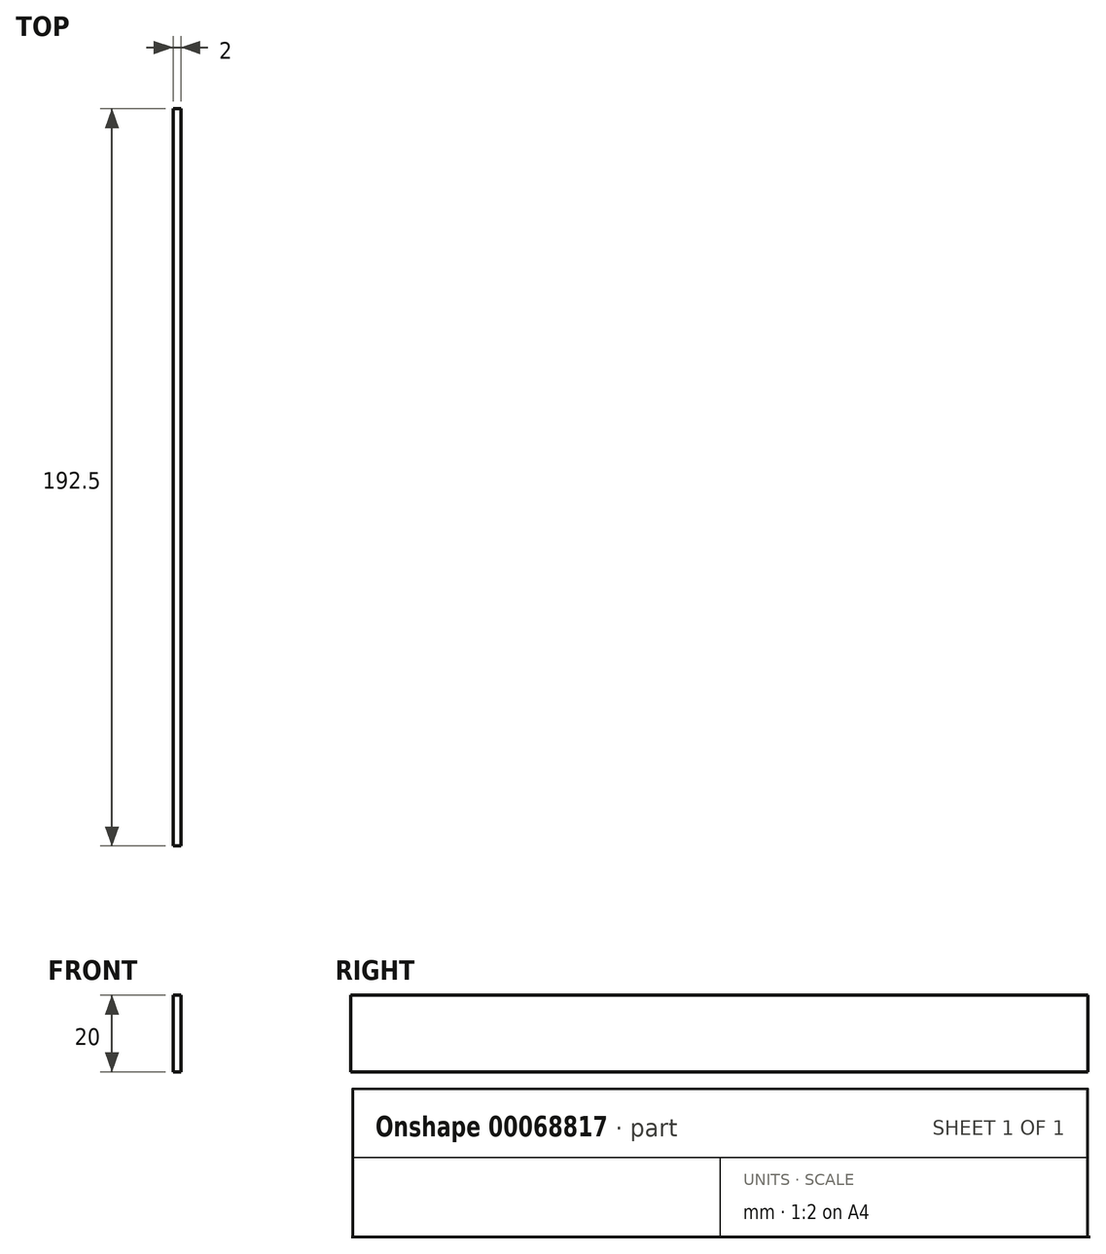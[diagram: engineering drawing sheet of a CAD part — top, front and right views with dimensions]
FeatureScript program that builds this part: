
annotation { "Feature Type Name" : "Feature", "Feature Type Description" : "" }
export const myFeature = defineFeature(function(context is Context, id is Id, definition is map)
    precondition{}
    {
        {
            var Q0;
            Q0=qCreatedBy(makeId("Right.planeOp"),FACE);
            var sketch = newSketch(context, id + "F0", { "sketchPlane" : qUnion([Q0])});
            skLineSegment(sketch, "E0.bottom", {"start": v(0, 0) * mm, "end": v(192.5, 0) * mm});
            skLineSegment(sketch, "E0.top", {"start": v(0, 20) * mm, "end": v(192.5, 20) * mm});
            skLineSegment(sketch, "E0.left", {"start": v(0, 0) * mm, "end": v(0, 20) * mm});
            skLineSegment(sketch, "E0.right", {"start": v(192.5, 0) * mm, "end": v(192.5, 20) * mm});
            skSolve(sketch);
        }
        {
            var Q0;
            Q0 = qSketchRegion(id + "F0", true);
            extrude(context, id + "F1", {"entities" : qUnion([Q0]), "depth" : 2 * mm});
        }
    });
